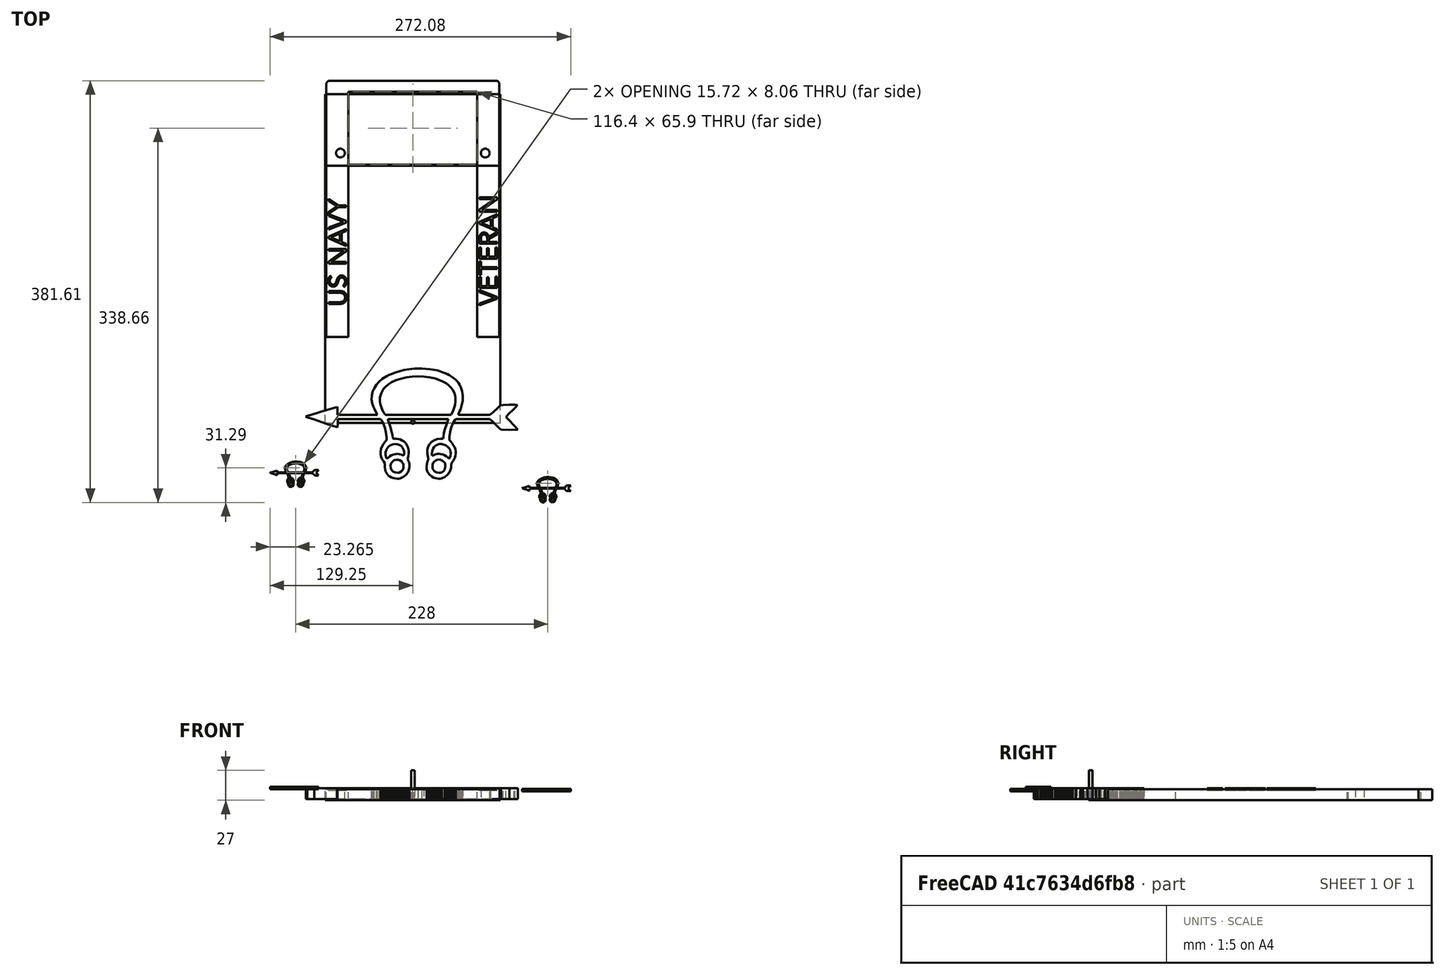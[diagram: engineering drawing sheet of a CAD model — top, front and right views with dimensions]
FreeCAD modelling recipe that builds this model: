
FCSTD DOCUMENT  (FreeCAD 0.22R36958 (Git))
Label: Frame-CNC-end
License: All rights reserved
LicenseURL: http://en.wikipedia.org/wiki/All_rights_reserved
objects: Part::FeaturePython×14, Path::FeaturePython×14, Part::Feature×5, Sketcher::SketchObject×4, PartDesign::Pad×4, PartDesign::Body×4, App::DocumentObjectGroup×3, Part::Part2DObjectPython×2, Part::Extrusion×2, Spreadsheet::Sheet×1, Mesh::Feature×1, PartDesign::AdditiveBox×1, PartDesign::SubtractiveCylinder×1, PartDesign::LinearPattern×1, App::FeaturePython×1
note: 45 computed .brp shape members not serialized (recipe doc carries the construction recipe); baked Part::Feature solids carry a one-line shape summary decoded from their .brp

FEATURE [Part::Part2DObjectPython] ShapeString  # Draft 2D object (typed FeaturePython)
  FontFile = /System/Library/Fonts/Avenir.ttc
  Fuse = false
  Justification = 4
  JustificationReference = 0
  KeepLeftMargin = false
  MakeFace = true
  ObliqueAngle = 0
  Placement = pos=(-68.2,154.4,10) rot=(0,0,1;1.5708rad)
  ScaleToSize = true
  Size = 16
  String = US NAVY
  Tracking = 1
  expr: .Placement.Base.x = -(<<vars>>.width - <<vars>>.top_banner_width) / 2
  expr: .Placement.Base.y = 152.13 + 2.27
  expr: .Placement.Base.z = <<vars>>.height
  expr: Size = <<vars>>.font_size
FEATURE [Spreadsheet::Sheet] Spreadsheet  label="vars"
  cells = A1='Length; B1(length)=308.8; C1==B1 / 2; D1='plate hole; E1(plate_hole)=7.9375; A2='Width; B2(width)=156.4; C2=160; D2='plate hole top left distance; E2(plate_hole_vertical)==length / 2 - 177.8 / 2; A3='material length; B3(material_length)=310; D3='plate hole horizontal_right; E3(plate_hole_horizontal_right)==(length - hole_distance_horizontal) / 2; A4='material_width; B4(material_width)=160; D4='plate hole horizontal left; E4(plate_hole_horizontal_left)==length / 2 - 88.9; A5='Font Size; B5(font_size)=16; D5='hole distance horizontal; E5(hole_distance_horizontal)=177.8; A6='Top banner width; B6(top_banner_width)=20; D6='hole distance vertical; E6(hole_distance_vertical)=120.65; A7='Bottom banner witdh; B7(bottom_banner_width)=20; A8='Height; B8(height)=10; A9='Guide hole distance; B9(guide_hole_length)=120; A10='Guide hole width; B10(guide_hole_width)=130; A11='hole distance from edge; B11(hole_distance_from_edge)=20; A12='hole size; B12(hole_size)=6.05; A13='template_length; B13(template_length)=155; A14='reference point; B14(reference_point)==first_cut; C14(second_cut)==(length - template_length) / 2 + template_length; D14(third_cut)==(length - template_length) / 2; E14(first_cut)==length; A15='side_width; B15(side_width)=10; A16='bit size; B16(bit_size)=3.175; A17='bridge width; B17(bridge_width)=1
FEATURE [Part::Part2DObjectPython] ShapeString001  # Draft 2D object (typed FeaturePython)
  FontFile = /System/Library/Fonts/Avenir.ttc
  Fuse = false
  Justification = 4
  JustificationReference = 0
  KeepLeftMargin = false
  MakeFace = true
  ObliqueAngle = 0
  Placement = pos=(68.2,154.395,10) rot=(0,0,1;1.5708rad)
  ScaleToSize = true
  Size = 16
  String = VETERAN
  Tracking = 0
  expr: .Placement.Base.x = (<<vars>>.width - <<vars>>.bottom_banner_width) / 2
  expr: .Placement.Base.y = 151.53 + 2.865
  expr: .Placement.Base.z = <<vars>>.height
  expr: Size = <<vars>>.font_size
FEATURE [Mesh::Feature] Sonar_Tech
FEATURE [Part::Feature] Sonar_Tech001
  Placement = pos=(0,0,10) rot=(0,0,1;0rad)
  shape: bbox 191.7 x 99.71 x 10 mm, 1500 faces, 0 solids (baked)
FEATURE [Part::Feature] Shell
  Placement = pos=(0,0,10) rot=(0,0,1;0rad)
  shape: bbox 191.7 x 99.71 x 10 mm, 373 faces, 0 solids (baked)
  expr: .Placement.Base.z = <<vars>>.height
FEATURE [Part::Feature] Scale_solid  label="Scale (Solid)"
  Placement = pos=(13,14,9) rot=(0,0,1;0rad)
  shape: bbox 44.08 x 22.93 x 2.3 mm, 373 faces (baked)
FEATURE [Part::Feature] Scale001_solid  label="Scale001 (Solid)"
  Placement = pos=(0,0,7) rot=(0,0,1;0rad)
  shape: bbox 44.08 x 22.93 x 2.3 mm, 373 faces (baked)
FEATURE [Sketcher::SketchObject] Sketch
  FullyConstrained = true
  MapMode = 5
  expr: Constraints[13] = <<vars>>.width / 2
  expr: Constraints[14] = <<vars>>.width
  expr: Constraints[23] = <<vars>>.top_banner_width
  expr: Constraints[24] = <<vars>>.bottom_banner_width
  expr: Constraints[25] = (<<vars>>.length - <<vars>>.template_length) / 2
  expr: Constraints[29] = <<vars>>.length + 10
  expr: Constraints[30] = (<<vars>>.length - <<vars>>.template_length) / 2 - <<vars>>.side_width - <<vars>>.bridge_width
  expr: Constraints[32] = <<vars>>.plate_hole
  expr: Constraints[33] = <<vars>>.plate_hole
  expr: Constraints[34] = <<vars>>.plate_hole_vertical
  expr: Constraints[35] = <<vars>>.plate_hole_vertical
  expr: Constraints[36] = <<vars>>.plate_hole_horizontal_left
  expr: Constraints[37] = <<vars>>.plate_hole_horizontal_left
  expr: Constraints[38] = <<vars>>.reference_point + 10
  expr: Constraints[39] = <<vars>>.reference_point + <<vars>>.side_width + 10
  sketch-geometry (13):
    g0: LineSegment StartX=78.2 StartY=76.9 StartZ=0 EndX=-78.2 EndY=76.9 EndZ=0
    g1: LineSegment StartX=-78.2 StartY=76.9 StartZ=0 EndX=-78.2 EndY=4 EndZ=0
    g2: ArcOfCircle CenterX=-74.2 CenterY=4 CenterZ=0 NormalX=0 NormalY=0 NormalZ=1 AngleXU=0 Radius=4 StartAngle=3.14159 EndAngle=4.71239
    g3: LineSegment StartX=-74.2 StartY=3e-16 StartZ=0 EndX=74.2 EndY=3e-16 EndZ=0
    g4: ArcOfCircle CenterX=74.2 CenterY=4 CenterZ=0 NormalX=0 NormalY=0 NormalZ=1 AngleXU=0 Radius=4 StartAngle=4.71239 EndAngle=6.28319
    g5: LineSegment StartX=78.2 StartY=4 StartZ=0 EndX=78.2 EndY=76.9 EndZ=0
    g6: LineSegment StartX=58.2 StartY=75.9 StartZ=0 EndX=-58.2 EndY=75.9 EndZ=0
    g7: LineSegment StartX=58.2 StartY=75.9 StartZ=0 EndX=58.2 EndY=10 EndZ=0
    g8: LineSegment StartX=58.2 StartY=10 StartZ=0 EndX=-58.2 EndY=10 EndZ=0
    g9: LineSegment StartX=-58.2 StartY=10 StartZ=0 EndX=-58.2 EndY=75.9 EndZ=0
    g10: GeomPoint X=0 Y=-318.8 Z=0
    g11: Circle CenterX=-65.5 CenterY=65.5 CenterZ=0 NormalX=0 NormalY=0 NormalZ=1 AngleXU=0 Radius=3.96875
    g12: Circle CenterX=65.5 CenterY=65.5 CenterZ=0 NormalX=0 NormalY=0 NormalZ=1 AngleXU=0 Radius=3.96875
  constraints (40):
    c: Vertical(g1)
    c: Coincident(g2,g3)
    c: Horizontal(g3)
    c: Tangent(g3,g4) = -1.5708
    c: Coincident(g4,g5)
    c: Vertical(g5)
    c: Horizontal(g8)
    c: Vertical(g9)
    c: Horizontal(g6)
    c: Vertical(g7)
    c: Equal(g2,g4)
    c: Angle(g2) = 1.5708
    c: Angle(g4) = 1.5708
    c: DistanceX(g0,g-1) = 78.2
    c: DistanceX(g0,g5) = 156.4
    c: Equal(g1,g5)
    c: Coincident(g2,g1)
    c: Horizontal(g0)
    c: DistanceX(g2) = -74.2
    c: Coincident(g1,g0)
    c: Coincident(g0,g5)
    c: Coincident(g9,g6)
    c: Coincident(g6,g7)
    c: Distance(g6,g1) = 20
    c: Distance(g6,g5) = 20
    c: Distance(g2,g0) = 76.9
    c: Coincident(g7,g8)
    c: Coincident(g9,g8)
    c: PointOnObject(g10,g-2)
    c: Distance(g-1,g10) = 318.8
    c: DistanceY(g9,g9) = 65.9
    c: DistanceY(g-1,g-1) = 0
    c: Diameter(g11) = 7.9375
    c: Diameter(g12) = 7.9375
    c: DistanceX(g11,g-1) = 65.5
    c: DistanceX(g-1,g12) = 65.5
    c: Distance(g11,g3) = 65.5
    c: Distance(g12,g3) = 65.5
    c: Distance(g10,g3) = 318.8
    c: Distance(g10,g8) = 328.8
FEATURE [PartDesign::Pad] Pad
  Direction = (0,0,1)
  Length = 10
  Length2 = 10
  Profile = -> Sketch
  ReferenceAxis = -> Sketch [N_Axis]
  Suppressed = false
  Type = 0
  expr: Length = <<vars>>.height
FEATURE [PartDesign::AdditiveBox] Box
  AttacherType = Attacher::AttachEngine3D
  AttachmentOffset = pos=(-55.025,13.175,0) rot=(0,0,1;0rad)
  AttachmentSupport = -> [XY_Plane]
  BaseFeature = -> Pad
  Height = 10
  Length = 110.05
  MapMode = 5
  Placement = pos=(-55.025,13.175,0) rot=(0,0,1;0rad)
  Suppressed = false
  Width = 282.45
  expr: .AttachmentOffset.Base.x = -<<vars>>.width / 2 + <<vars>>.top_banner_width + <<vars>>.bit_size
  expr: .AttachmentOffset.Base.y = <<vars>>.reference_point - <<vars>>.length + <<vars>>.side_width + <<vars>>.bit_size
  expr: Height = <<vars>>.height
  expr: Length = <<vars>>.width - <<vars>>.top_banner_width - <<vars>>.bottom_banner_width - <<vars>>.bit_size * 2
  expr: Width = <<vars>>.length - <<vars>>.side_width * 2 - <<vars>>.bit_size * 2
FEATURE [Sketcher::SketchObject] Sketch001
  FullyConstrained = true
  MapMode = 5
  expr: Constraints[18] = <<vars>>.width
  expr: Constraints[23] = <<vars>>.top_banner_width
  expr: Constraints[24] = <<vars>>.bottom_banner_width
  expr: Constraints[25] = -<<vars>>.width / 2
  expr: Constraints[26] = (<<vars>>.length - <<vars>>.template_length) / 2
  expr: Constraints[28] = <<vars>>.plate_hole
  expr: Constraints[30] = <<vars>>.plate_hole_vertical
  expr: Constraints[31] = <<vars>>.plate_hole_vertical
  expr: Constraints[32] = <<vars>>.plate_hole_horizontal_right
  expr: Constraints[34] = <<vars>>.length + <<vars>>.reference_point
  expr: Constraints[35] = <<vars>>.length
  expr: Constraints[36] = <<vars>>.length - <<vars>>.side_width + <<vars>>.reference_point
  expr: Constraints[37] = <<vars>>.length - (<<vars>>.length - <<vars>>.template_length) / 2 + <<vars>>.bridge_width + <<vars>>.reference_point
  sketch-geometry (13):
    g0: LineSegment StartX=-78.2 StartY=231.9 StartZ=0 EndX=-78.2 EndY=305.8 EndZ=0
    g1: ArcOfCircle CenterX=-75.2 CenterY=305.8 CenterZ=0 NormalX=0 NormalY=0 NormalZ=1 AngleXU=0 Radius=3 StartAngle=1.5708 EndAngle=3.14159
    g2: LineSegment StartX=-75.2 StartY=308.8 StartZ=0 EndX=75.2 EndY=308.8 EndZ=0
    g3: ArcOfCircle CenterX=75.2 CenterY=305.8 CenterZ=0 NormalX=0 NormalY=0 NormalZ=1 AngleXU=0 Radius=3 StartAngle=3.8e-15 EndAngle=1.5708
    g4: LineSegment StartX=78.2 StartY=305.8 StartZ=0 EndX=78.2 EndY=231.9 EndZ=0
    g5: LineSegment StartX=78.2 StartY=231.9 StartZ=0 EndX=-78.2 EndY=231.9 EndZ=0
    g6: LineSegment StartX=-58.2 StartY=232.9 StartZ=0 EndX=58.2 EndY=232.9 EndZ=0
    g7: LineSegment StartX=58.2 StartY=232.9 StartZ=0 EndX=58.2 EndY=298.8 EndZ=0
    g8: LineSegment StartX=58.2 StartY=298.8 StartZ=0 EndX=-58.2 EndY=298.8 EndZ=0
    g9: LineSegment StartX=-58.2 StartY=298.8 StartZ=0 EndX=-58.2 EndY=232.9 EndZ=0
    g10: Circle CenterX=-65.5 CenterY=243.3 CenterZ=0 NormalX=0 NormalY=0 NormalZ=1 AngleXU=0 Radius=3.96875
    g11: Circle CenterX=65.5 CenterY=243.3 CenterZ=0 NormalX=0 NormalY=0 NormalZ=1 AngleXU=0 Radius=3.96875
    g12: GeomPoint X=0 Y=-308.8 Z=0
  constraints (38):
    c: Tangent(g0,g1) = 1.5708
    c: Coincident(g1,g2)
    c: Horizontal(g2)
    c: Tangent(g2,g3) = 1.5708
    c: Coincident(g3,g4)
    c: Vertical(g4)
    c: Coincident(g4,g5)
    c: Coincident(g5,g0)
    c: Horizontal(g5)
    c: Coincident(g6,g7)
    c: Coincident(g7,g8)
    c: Coincident(g8,g9)
    c: Coincident(g9,g6)
    c: Horizontal(g6)
    c: Horizontal(g8)
    c: Vertical(g7)
    c: Vertical(g9)
    c: Vertical(g0)
    c: DistanceX(g5,g5) = 156.4
    c: Angle(g1) = 1.5708
    c: Angle(g3) = 1.5708
    c: Diameter(g1) = 6
    c: Diameter(g3) = 6
    c: Distance(g6,g0) = 20
    c: Distance(g6,g4) = 20
    c: DistanceX(g-2,g0) = -78.2
    c: Distance(g4,g2) = 76.9
    c: Equal(g11,g10)
    c: Diameter(g11) = 7.9375
    c: Horizontal(g10,g11)
    c: DistanceX(g10,g-1) = 65.5
    c: DistanceX(g-1,g11) = 65.5
    c: Distance(g10,g2) = 65.5
    c: PointOnObject(g12,g-2)
    c: Distance(g12,g2) = 617.6
    c: DistanceY(g12,g-1) = 308.8
    c: Distance(g12,g8) = 607.6
    c: Distance(g12,g6) = 541.7
FEATURE [PartDesign::Pad] Pad001
  Direction = (0,0,1)
  Length = 10
  Length2 = 10
  Profile = -> Sketch001
  ReferenceAxis = -> Sketch001 [N_Axis]
  Suppressed = false
  Type = 0
  expr: Length = <<vars>>.height
FEATURE [PartDesign::Body] Body001
  Group = -> [Sketch001,Pad001]
  Origin = -> Origin001
  Tip = -> Pad001
FEATURE [Part::Feature] Sonar_Tech001_solid  label="Sonar_Tech001 (Solid)"
  Placement = pos=(0,0,1) rot=(0,0,1;0rad)
  shape: bbox 191.7 x 99.71 x 10 mm, 1500 faces (baked)
FEATURE [Part::Extrusion] Extrude
  Base = -> ShapeString
  Dir = (0,0,1)
  DirMode = 2
  FaceMakerClass = Part::FaceMakerBullseye
  LengthFwd = 2
  LengthRev = 0
  Solid = false
  Symmetric = true
FEATURE [Part::Extrusion] Extrude001
  Base = -> ShapeString001
  Dir = (0,0,1)
  DirMode = 2
  FaceMakerClass = Part::FaceMakerBullseye
  LengthFwd = 2
  LengthRev = 0
  Solid = false
  Symmetric = true
FEATURE [Sketcher::SketchObject] Sketch002
  FullyConstrained = true
  MapMode = 5
  expr: Constraints[10] = -<<vars>>.width / 2
  expr: Constraints[12] = <<vars>>.length
  expr: Constraints[13] = (<<vars>>.length - <<vars>>.template_length) / 2 + <<vars>>.reference_point
  expr: Constraints[8] = <<vars>>.top_banner_width
  expr: Constraints[9] = <<vars>>.template_length
  sketch-geometry (5):
    g0: LineSegment StartX=-78.2 StartY=231.9 StartZ=0 EndX=-78.2 EndY=76.9 EndZ=0
    g1: LineSegment StartX=-78.2 StartY=76.9 StartZ=0 EndX=-58.2 EndY=76.9 EndZ=0
    g2: LineSegment StartX=-58.2 StartY=76.9 StartZ=0 EndX=-58.2 EndY=231.9 EndZ=0
    g3: LineSegment StartX=-58.2 StartY=231.9 StartZ=0 EndX=-78.2 EndY=231.9 EndZ=0
    g4: GeomPoint X=0 Y=-308.8 Z=0
  constraints (14):
    c: Coincident(g0,g1)
    c: Coincident(g1,g2)
    c: Coincident(g2,g3)
    c: Coincident(g3,g0)
    c: Vertical(g0)
    c: Vertical(g2)
    c: Horizontal(g1)
    c: Horizontal(g3)
    c: DistanceX(g3,g3) = 20
    c: DistanceY(g0,g0) = 155
    c: DistanceX(g-2,g0) = -78.2
    c: PointOnObject(g4,g-2)
    c: DistanceY(g4,g-1) = 308.8
    c: DistanceY(g4,g1) = 385.7
FEATURE [PartDesign::Pad] Pad002
  Direction = (0,0,1)
  Length = 10
  Length2 = 10
  Profile = -> Sketch002
  ReferenceAxis = -> Sketch002 [N_Axis]
  Suppressed = false
  Type = 0
  expr: Length = <<vars>>.height
FEATURE [PartDesign::Body] Body002
  Group = -> [Sketch002,Pad002]
  Origin = -> Origin002
  Tip = -> Pad002
FEATURE [Sketcher::SketchObject] Sketch003
  FullyConstrained = true
  MapMode = 5
  expr: Constraints[11] = <<vars>>.length
  expr: Constraints[12] = <<vars>>.width / 2
  expr: Constraints[13] = (<<vars>>.length - <<vars>>.template_length) / 2 + <<vars>>.reference_point
  expr: Constraints[8] = <<vars>>.bottom_banner_width
  expr: Constraints[9] = <<vars>>.template_length
  sketch-geometry (5):
    g0: LineSegment StartX=58.2 StartY=231.9 StartZ=0 EndX=58.2 EndY=76.9 EndZ=0
    g1: LineSegment StartX=58.2 StartY=76.9 StartZ=0 EndX=78.2 EndY=76.9 EndZ=0
    g2: LineSegment StartX=78.2 StartY=76.9 StartZ=0 EndX=78.2 EndY=231.9 EndZ=0
    g3: LineSegment StartX=78.2 StartY=231.9 StartZ=0 EndX=58.2 EndY=231.9 EndZ=0
    g4: GeomPoint X=0 Y=-308.8 Z=0
  constraints (14):
    c: Coincident(g0,g1)
    c: Coincident(g1,g2)
    c: Coincident(g2,g3)
    c: Coincident(g3,g0)
    c: Vertical(g0)
    c: Vertical(g2)
    c: Horizontal(g1)
    c: Horizontal(g3)
    c: DistanceX(g3,g3) = 20
    c: DistanceY(g2,g2) = 155
    c: PointOnObject(g4,g-2)
    c: DistanceY(g4,g-1) = 308.8
    c: DistanceX(g-1,g2) = 78.2
    c: DistanceY(g4,g0) = 385.7
FEATURE [PartDesign::Pad] Pad003
  Direction = (0,0,1)
  Length = 10
  Length2 = 10
  Profile = -> Sketch003
  ReferenceAxis = -> Sketch003 [N_Axis]
  Suppressed = false
  Type = 0
  expr: Length = <<vars>>.height
FEATURE [PartDesign::Body] Body003
  Group = -> [Sketch003,Pad003]
  Origin = -> Origin003
  Tip = -> Pad003
FEATURE [PartDesign::SubtractiveCylinder] Cylinder
  Angle = 360
  AttacherType = Attacher::AttachEngine3D
  AttachmentOffset = pos=(55.025,10,-10) rot=(0,0,1;0rad)
  AttachmentSupport = -> [Box]
  BaseFeature = -> Box
  FirstAngle = 0
  Height = 10
  MapMode = 5
  Placement = pos=(0,23.175,0) rot=(0,0,1;0rad)
  Radius = 3.03
  SecondAngle = 0
  Suppressed = false
  expr: .AttachmentOffset.Base.x = Box.Length / 2
  expr: .AttachmentOffset.Base.y = <<vars>>.side_width
  expr: .AttachmentOffset.Base.z = -Height
  expr: Height = <<vars>>.height
  expr: Radius = 3.03
FEATURE [PartDesign::LinearPattern] LinearPattern
  BaseFeature = -> Cylinder
  Direction = -> Y_Axis
  Length = 75.91
  Mode = 1
  Occurrences = 2
  Offset = 75.91
  Originals = -> [Cylinder]
  Placement = pos=(0,23.175,0) rot=(0,0,1;0rad)
  Suppressed = false
  expr: Offset = 75.91 mm
FEATURE [PartDesign::Body] Body
  Group = -> [Sketch,Pad,Box,Cylinder,LinearPattern]
  Origin = -> Origin
  Tip = -> Cylinder
FEATURE [App::FeaturePython] SetupSheet  # Path/CAM operation (typed FeaturePython)
  ClearanceHeightExpression = OpStockZMax+SetupSheet.ClearanceHeightOffset
  ClearanceHeightOffset = 5
  CoolantMode = 0
  CoolantModes = None | Flood | Mist
  FinalDepthExpression = OpFinalDepth
  HorizRapid = 0
  SafeHeightExpression = OpStockZMax+SetupSheet.SafeHeightOffset
  SafeHeightOffset = 3
  StartDepthExpression = OpStartDepth
  StepDownExpression = OpToolDiameter
  VertRapid = 0
FEATURE [Part::FeaturePython] Clone  label="Model-Body"  # Draft clone (typed FeaturePython)
  AttacherType = Attacher::AttachEngine3D
  Fuse = false
  Objects = -> [Body]
  PathResource = Model
  Scale = (1,1,1)
FEATURE [App::DocumentObjectGroup] Model
  Group = -> [Clone]
FEATURE [Part::FeaturePython] ToolBit  label="0.8mm_Endmill004"  # Path/CAM toolbit (typed FeaturePython)
  BitPropertyNames = Chipload | CuttingEdgeHeight | Diameter | Flutes | Length | Material | ShankDiameter | SpindleDirection
  BitShape = /private/var/folders/4z/cpn_82wx3qz0m4lfqxz9fps80000gn/T/AppTranslocation/590B87E8-BEDD-40D1-A770-7063B047F674/d/FreeCAD.app/Contents/Resources/Mod/CAM/Tools/Shape/endmill.fcstd
  Chipload = 0
  CuttingEdgeHeight = 10
  Diameter = 0.8
  Flutes = 0
  Length = 27
  Material = 0
  ShankDiameter = 3.17
  ShapeName = endmill
  SpindleDirection = 0
FEATURE [Path::FeaturePython] __8mm_Endmill001  label="0.8mm_Endmill002"  # Path/CAM operation (typed FeaturePython)
  HorizFeed = 3.33333
  HorizRapid = 0
  SpindleDir = 0
  SpindleSpeed = 2000
  Tool = -> ToolBit
  ToolNumber = 2
  VertFeed = 3.33333
  VertRapid = 0
  expr: HorizRapid = SetupSheet.HorizRapid
  expr: VertRapid = SetupSheet.VertRapid
FEATURE [Part::FeaturePython] ToolBit001  label="1.0mm_Endmill003"  # Path/CAM toolbit (typed FeaturePython)
  BitPropertyNames = Chipload | CuttingEdgeHeight | Diameter | Flutes | Length | Material | ShankDiameter | SpindleDirection
  BitShape = /private/var/folders/4z/cpn_82wx3qz0m4lfqxz9fps80000gn/T/AppTranslocation/590B87E8-BEDD-40D1-A770-7063B047F674/d/FreeCAD.app/Contents/Resources/Mod/CAM/Tools/Shape/endmill.fcstd
  Chipload = 0
  CuttingEdgeHeight = 10
  Diameter = 1
  Flutes = 0
  Length = 27
  Material = 0
  ShankDiameter = 3.17
  ShapeName = endmill
  SpindleDirection = 0
FEATURE [Path::FeaturePython] __0mm_Endmill001  label="1.0mm_Endmill002"  # Path/CAM operation (typed FeaturePython)
  HorizFeed = 3.33333
  HorizRapid = 0
  SpindleDir = 0
  SpindleSpeed = 2000
  Tool = -> ToolBit001
  ToolNumber = 3
  VertFeed = 3.33333
  VertRapid = 0
  expr: HorizRapid = SetupSheet.HorizRapid
  expr: VertRapid = SetupSheet.VertRapid
FEATURE [Part::FeaturePython] ToolBit002  label="1.2mm_endmill003"  # Path/CAM toolbit (typed FeaturePython)
  BitPropertyNames = Chipload | CuttingEdgeHeight | Diameter | Flutes | Length | Material | ShankDiameter | SpindleDirection
  BitShape = /private/var/folders/4z/cpn_82wx3qz0m4lfqxz9fps80000gn/T/AppTranslocation/590B87E8-BEDD-40D1-A770-7063B047F674/d/FreeCAD.app/Contents/Resources/Mod/CAM/Tools/Shape/endmill.fcstd
  Chipload = 0
  CuttingEdgeHeight = 10
  Diameter = 1.2
  Flutes = 0
  Length = 27
  Material = 0
  ShankDiameter = 3.13
  ShapeName = endmill
  SpindleDirection = 0
FEATURE [Path::FeaturePython] __2mm_endmill001  label="1.2mm_endmill002"  # Path/CAM operation (typed FeaturePython)
  HorizFeed = 3.33333
  HorizRapid = 0
  SpindleDir = 0
  SpindleSpeed = 2000
  Tool = -> ToolBit002
  ToolNumber = 4
  VertFeed = 3.33333
  VertRapid = 0
  expr: HorizRapid = SetupSheet.HorizRapid
  expr: VertRapid = SetupSheet.VertRapid
FEATURE [Part::FeaturePython] ToolBit003  label="1.4mm_Endmill003"  # Path/CAM toolbit (typed FeaturePython)
  BitPropertyNames = Chipload | CuttingEdgeHeight | Diameter | Flutes | Length | Material | ShankDiameter | SpindleDirection
  BitShape = /private/var/folders/4z/cpn_82wx3qz0m4lfqxz9fps80000gn/T/AppTranslocation/590B87E8-BEDD-40D1-A770-7063B047F674/d/FreeCAD.app/Contents/Resources/Mod/CAM/Tools/Shape/endmill.fcstd
  Chipload = 0
  CuttingEdgeHeight = 10
  Diameter = 1.4
  Flutes = 0
  Length = 27
  Material = 0
  ShankDiameter = 3.17
  ShapeName = endmill
  SpindleDirection = 0
FEATURE [Path::FeaturePython] __4mm_Endmill001  label="1.4mm_Endmill002"  # Path/CAM operation (typed FeaturePython)
  HorizFeed = 3.33333
  HorizRapid = 0
  SpindleDir = 0
  SpindleSpeed = 2000
  Tool = -> ToolBit003
  ToolNumber = 5
  VertFeed = 3.33333
  VertRapid = 0
  expr: HorizRapid = SetupSheet.HorizRapid
  expr: VertRapid = SetupSheet.VertRapid
FEATURE [Part::FeaturePython] ToolBit004  label="1.8mm_Endmill"  # Path/CAM toolbit (typed FeaturePython)
  BitPropertyNames = Chipload | CuttingEdgeHeight | Diameter | Flutes | Length | Material | ShankDiameter | SpindleDirection
  BitShape = /private/var/folders/4z/cpn_82wx3qz0m4lfqxz9fps80000gn/T/AppTranslocation/590B87E8-BEDD-40D1-A770-7063B047F674/d/FreeCAD.app/Contents/Resources/Mod/CAM/Tools/Shape/endmill.fcstd
  Chipload = 0
  CuttingEdgeHeight = 10
  Diameter = 1.8
  Flutes = 0
  Length = 27
  Material = 0
  ShankDiameter = 3.17
  ShapeName = endmill
  SpindleDirection = 0
FEATURE [Path::FeaturePython] __8mm_Endmill002  label="1.8mm_Endmill001"  # Path/CAM operation (typed FeaturePython)
  HorizFeed = 3.33333
  HorizRapid = 0
  SpindleDir = 0
  SpindleSpeed = 2000
  Tool = -> ToolBit004
  ToolNumber = 7
  VertFeed = 3.33333
  VertRapid = 0
  expr: HorizRapid = SetupSheet.HorizRapid
  expr: VertRapid = SetupSheet.VertRapid
FEATURE [Part::FeaturePython] ToolBit005  label="2.0mm_Endmill"  # Path/CAM toolbit (typed FeaturePython)
  BitPropertyNames = Chipload | CuttingEdgeHeight | Diameter | Flutes | Length | Material | ShankDiameter | SpindleDirection
  BitShape = /private/var/folders/4z/cpn_82wx3qz0m4lfqxz9fps80000gn/T/AppTranslocation/590B87E8-BEDD-40D1-A770-7063B047F674/d/FreeCAD.app/Contents/Resources/Mod/CAM/Tools/Shape/endmill.fcstd
  Chipload = 0
  CuttingEdgeHeight = 10
  Diameter = 2
  Flutes = 0
  Length = 27
  Material = 0
  ShankDiameter = 3.17
  ShapeName = endmill
  SpindleDirection = 0
FEATURE [Path::FeaturePython] __0mm_Endmill002  label="2.0mm_Endmill001"  # Path/CAM operation (typed FeaturePython)
  HorizFeed = 3.33333
  HorizRapid = 0
  SpindleDir = 0
  SpindleSpeed = 2000
  Tool = -> ToolBit005
  ToolNumber = 8
  VertFeed = 3.33333
  VertRapid = 0
  expr: HorizRapid = SetupSheet.HorizRapid
  expr: VertRapid = SetupSheet.VertRapid
FEATURE [Part::FeaturePython] ToolBit006  label="2.2mm_Endmill"  # Path/CAM toolbit (typed FeaturePython)
  BitPropertyNames = Chipload | CuttingEdgeHeight | Diameter | Flutes | Length | Material | ShankDiameter | SpindleDirection
  BitShape = /private/var/folders/4z/cpn_82wx3qz0m4lfqxz9fps80000gn/T/AppTranslocation/590B87E8-BEDD-40D1-A770-7063B047F674/d/FreeCAD.app/Contents/Resources/Mod/CAM/Tools/Shape/endmill.fcstd
  Chipload = 0
  CuttingEdgeHeight = 10
  Diameter = 2.2
  Flutes = 0
  Length = 27
  Material = 0
  ShankDiameter = 3.17
  ShapeName = endmill
  SpindleDirection = 0
FEATURE [Path::FeaturePython] __2mm_Endmill  label="2.2mm_Endmill001"  # Path/CAM operation (typed FeaturePython)
  HorizFeed = 3.33333
  HorizRapid = 0
  SpindleDir = 0
  SpindleSpeed = 2000
  Tool = -> ToolBit006
  ToolNumber = 9
  VertFeed = 3.33333
  VertRapid = 0
  expr: HorizRapid = SetupSheet.HorizRapid
  expr: VertRapid = SetupSheet.VertRapid
FEATURE [Part::FeaturePython] ToolBit007  label="2.4mm_Endmill"  # Path/CAM toolbit (typed FeaturePython)
  BitPropertyNames = Chipload | CuttingEdgeHeight | Diameter | Flutes | Length | Material | ShankDiameter | SpindleDirection
  BitShape = /private/var/folders/4z/cpn_82wx3qz0m4lfqxz9fps80000gn/T/AppTranslocation/590B87E8-BEDD-40D1-A770-7063B047F674/d/FreeCAD.app/Contents/Resources/Mod/CAM/Tools/Shape/endmill.fcstd
  Chipload = 0
  CuttingEdgeHeight = 10
  Diameter = 2.4
  Flutes = 0
  Length = 27
  Material = 0
  ShankDiameter = 3.17
  ShapeName = endmill
  SpindleDirection = 0
FEATURE [Path::FeaturePython] __4mm_Endmill002  label="2.4mm_Endmill001"  # Path/CAM operation (typed FeaturePython)
  HorizFeed = 3.33333
  HorizRapid = 0
  SpindleDir = 0
  SpindleSpeed = 2000
  Tool = -> ToolBit007
  ToolNumber = 10
  VertFeed = 3.33333
  VertRapid = 0
  expr: HorizRapid = SetupSheet.HorizRapid
  expr: VertRapid = SetupSheet.VertRapid
FEATURE [Part::FeaturePython] ToolBit008  label="2.6mm_Endmill"  # Path/CAM toolbit (typed FeaturePython)
  BitPropertyNames = Chipload | CuttingEdgeHeight | Diameter | Flutes | Length | Material | ShankDiameter | SpindleDirection
  BitShape = /private/var/folders/4z/cpn_82wx3qz0m4lfqxz9fps80000gn/T/AppTranslocation/590B87E8-BEDD-40D1-A770-7063B047F674/d/FreeCAD.app/Contents/Resources/Mod/CAM/Tools/Shape/endmill.fcstd
  Chipload = 0
  CuttingEdgeHeight = 10
  Diameter = 2.6
  Flutes = 0
  Length = 27
  Material = 0
  ShankDiameter = 3.17
  ShapeName = endmill
  SpindleDirection = 0
FEATURE [Path::FeaturePython] __6mm_Endmill  label="2.6mm_Endmill001"  # Path/CAM operation (typed FeaturePython)
  HorizFeed = 3.33333
  HorizRapid = 0
  SpindleDir = 0
  SpindleSpeed = 2000
  Tool = -> ToolBit008
  ToolNumber = 11
  VertFeed = 3.33333
  VertRapid = 0
  expr: HorizRapid = SetupSheet.HorizRapid
  expr: VertRapid = SetupSheet.VertRapid
FEATURE [Part::FeaturePython] ToolBit009  label="2.8mm_Endmill"  # Path/CAM toolbit (typed FeaturePython)
  BitPropertyNames = Chipload | CuttingEdgeHeight | Diameter | Flutes | Length | Material | ShankDiameter | SpindleDirection
  BitShape = /private/var/folders/4z/cpn_82wx3qz0m4lfqxz9fps80000gn/T/AppTranslocation/590B87E8-BEDD-40D1-A770-7063B047F674/d/FreeCAD.app/Contents/Resources/Mod/CAM/Tools/Shape/endmill.fcstd
  Chipload = 0
  CuttingEdgeHeight = 10
  Diameter = 2.8
  Flutes = 0
  Length = 27
  Material = 0
  ShankDiameter = 3.17
  ShapeName = endmill
  SpindleDirection = 0
FEATURE [Path::FeaturePython] __8mm_Endmill003  label="2.8mm_Endmill001"  # Path/CAM operation (typed FeaturePython)
  HorizFeed = 3.33333
  HorizRapid = 0
  SpindleDir = 0
  SpindleSpeed = 2000
  Tool = -> ToolBit009
  ToolNumber = 12
  VertFeed = 3.33333
  VertRapid = 0
  expr: HorizRapid = SetupSheet.HorizRapid
  expr: VertRapid = SetupSheet.VertRapid
FEATURE [Part::FeaturePython] ToolBit010  label="3.0mm_Endmill"  # Path/CAM toolbit (typed FeaturePython)
  BitPropertyNames = Chipload | CuttingEdgeHeight | Diameter | Flutes | Length | Material | ShankDiameter | SpindleDirection
  BitShape = /private/var/folders/4z/cpn_82wx3qz0m4lfqxz9fps80000gn/T/AppTranslocation/590B87E8-BEDD-40D1-A770-7063B047F674/d/FreeCAD.app/Contents/Resources/Mod/CAM/Tools/Shape/endmill.fcstd
  Chipload = 0
  CuttingEdgeHeight = 10
  Diameter = 3
  Flutes = 0
  Length = 27
  Material = 0
  ShankDiameter = 3.17
  ShapeName = endmill
  SpindleDirection = 0
FEATURE [Path::FeaturePython] __0mm_Endmill003  label="3.0mm_Endmill001"  # Path/CAM operation (typed FeaturePython)
  HorizFeed = 3.33333
  HorizRapid = 0
  SpindleDir = 0
  SpindleSpeed = 2000
  Tool = -> ToolBit010
  ToolNumber = 13
  VertFeed = 3.33333
  VertRapid = 0
  expr: HorizRapid = SetupSheet.HorizRapid
  expr: VertRapid = SetupSheet.VertRapid
FEATURE [Part::FeaturePython] ToolBit011  label="3.175mm_endmill009"  # Path/CAM toolbit (typed FeaturePython)
  BitPropertyNames = Chipload | CuttingEdgeHeight | Diameter | Flutes | Length | Material | ShankDiameter | SpindleDirection
  BitShape = /private/var/folders/4z/cpn_82wx3qz0m4lfqxz9fps80000gn/T/AppTranslocation/590B87E8-BEDD-40D1-A770-7063B047F674/d/FreeCAD.app/Contents/Resources/Mod/CAM/Tools/Shape/endmill.fcstd
  Chipload = 0
  CuttingEdgeHeight = 10
  Diameter = 3.17
  Flutes = 0
  Length = 27
  Material = 0
  ShankDiameter = 3.17
  ShapeName = endmill
  SpindleDirection = 0
FEATURE [Path::FeaturePython] __175mm_endmill007  label="3.175mm_endmill008"  # Path/CAM operation (typed FeaturePython)
  HorizFeed = 3.33333
  HorizRapid = 0
  SpindleDir = 0
  SpindleSpeed = 2000
  Tool = -> ToolBit011
  ToolNumber = 6
  VertFeed = 3.33333
  VertRapid = 0
  expr: HorizRapid = SetupSheet.HorizRapid
  expr: VertRapid = SetupSheet.VertRapid
FEATURE [App::DocumentObjectGroup] Tools
  Group = -> [__8mm_Endmill001,__0mm_Endmill001,__2mm_endmill001,__4mm_Endmill001,__8mm_Endmill002,__0mm_Endmill002,__2mm_Endmill,__4mm_Endmill002,__6mm_Endmill,__8mm_Endmill003,__0mm_Endmill003,__175mm_endmill007]
FEATURE [Part::FeaturePython] Stock  # WARN: FeaturePython — macro-defined, semantics opaque (R4)
  Base = -> Model
  ExtXneg = 1
  ExtXpos = 1
  ExtYneg = 1
  ExtYpos = 1
  ExtZneg = 0
  ExtZpos = 0
  Placement = pos=(-78.2,0,0) rot=(0,0,1;0rad)
  StockType = FromBase
FEATURE [Path::FeaturePython] Profile  # Path/CAM operation (typed FeaturePython)
  Active = true
  AreaParams:
    Tolerance = 1e-07
    FitArcs = True
    Simplify = False
    CleanDistance = 0.0
    Accuracy = 0.01
    Unit = 1.0
    MinArcPoints = 4
    MaxArcPoints = 100
    ClipperScale = 10000000.0
    Fill = 0
    Coplanar = 0
    Reorient = True
    Outline = False
    Explode = False
    OpenMode = 0
    Deflection = 0.01
    SubjectFill = 0
    ClipFill = 0
    Offset = -1.585
    ExtraPass = 0
    Stepover = 0.0
    LastStepover = 0.0
    JoinType = 0
    EndType = 0
    MiterLimit = 2.0
    RoundPrecision = 0.0
    PocketMode = 0
    ToolRadius = 1.0
    PocketExtraOffset = 0.0
    PocketStepover = 0.0
    PocketLastStepover = 0.0
    FromCenter = False
    Angle = 45.0
    AngleShift = 0.0
    Shift = 0.0
    Thicken = False
    SectionCount = -1
    Stepdown = 1.0
    SectionOffset = 0.0
    SectionTolerance = 1e-06
    SectionMode = 2
    Project = False
  Base = -> [Clone]
  ClearanceHeight = 15
  CoolantMode = 0
  CycleTime = 00:03:57
  Direction = 0
  FinalDepth = 10
  HandleMultipleFeatures = 0
  JoinType = 0
  MiterLimit = 0.1
  OffsetExtra = 0
  OpFinalDepth = 10
  OpStartDepth = 13.17
  OpStockZMax = 10
  OpStockZMin = 0
  OpToolDiameter = 3.17
  PathParams = {'orientation': 1, 'feedrate': 3.3333333333333335, 'feedrate_v': 3.3333333333333335, 'verbose': True, 'resume_height': 13.0, 'retraction': 15.0, 'return_end': True, 'preamble': False, 'start': Vector (63.673808577552705, 63.973210460148664, 15.0)}
  SafeHeight = 13
  Side = 1
  SplitArcs = false
  StartDepth = 13.17
  StartPoint = (0,0,0)
  StepDown = 3.17
  ToolController = -> __175mm_endmill007
  UseComp = true
  UseStartPoint = false
  processCircles = false
  processHoles = false
  processPerimeter = true
  expr: ClearanceHeight = OpStockZMax + SetupSheet.ClearanceHeightOffset
  expr: FinalDepth = OpFinalDepth
  expr: SafeHeight = OpStockZMax + SetupSheet.SafeHeightOffset
  expr: StartDepth = OpStartDepth
  expr: StepDown = OpToolDiameter
FEATURE [App::DocumentObjectGroup] Operations
  Group = -> [Profile]
FEATURE [Path::FeaturePython] Job  # Path/CAM operation (typed FeaturePython)
  CycleTime = 00:03:57
  Fixtures = G54
  GeometryTolerance = 0.01
  JobType = 0
  Model = -> Model
  Operations = -> Operations
  OrderOutputBy = 0
  PostProcessor = 1
  SetupSheet = -> SetupSheet
  SplitOutput = false
  Stock = -> Stock
  Tools = -> Tools
